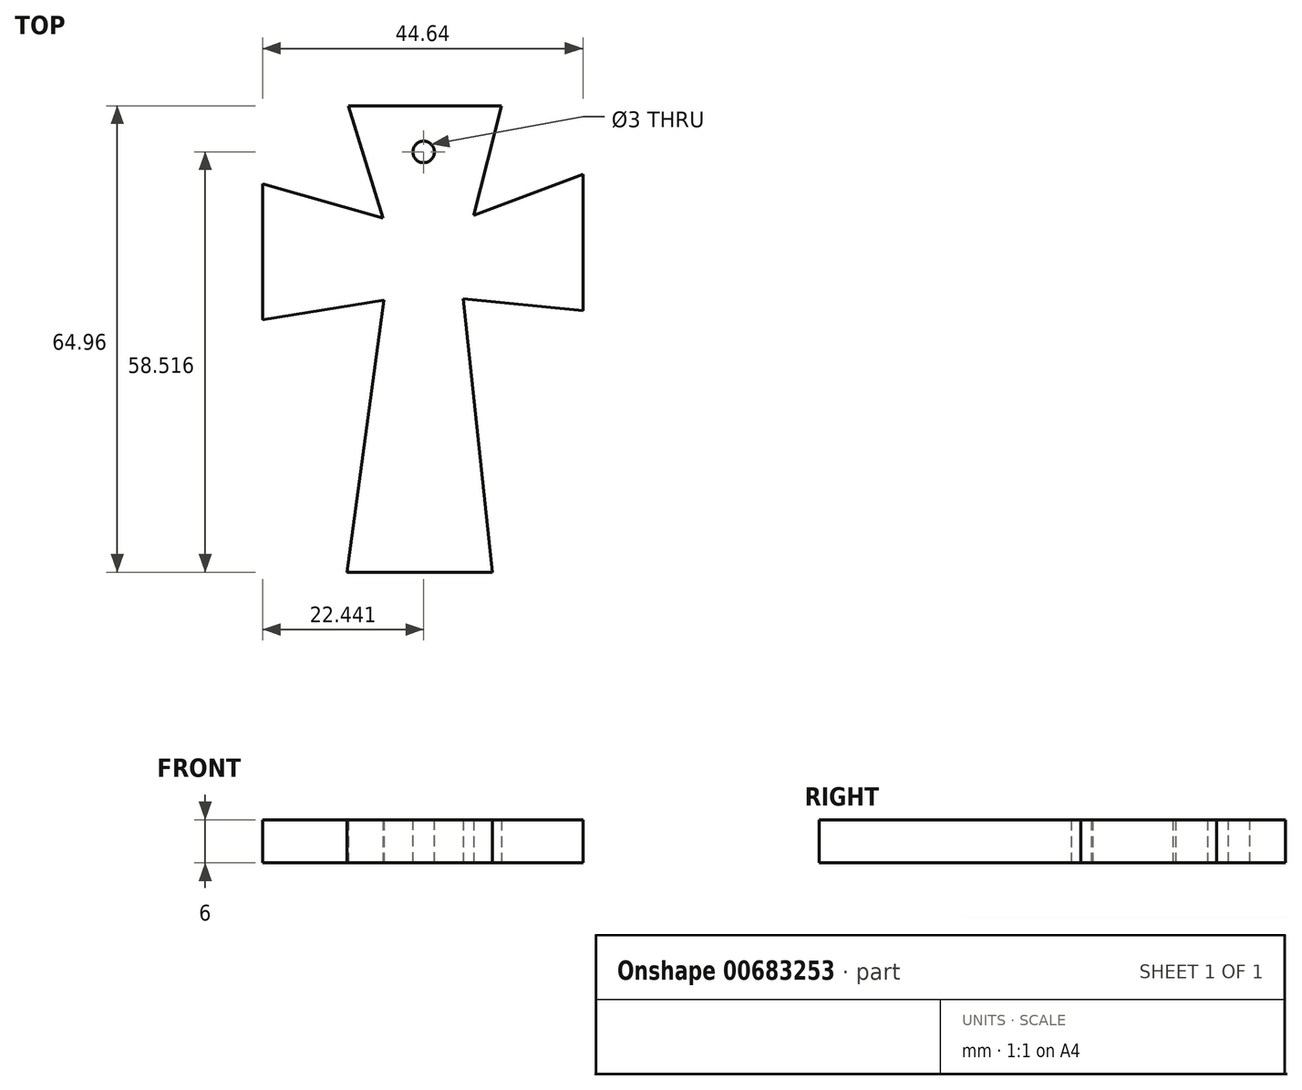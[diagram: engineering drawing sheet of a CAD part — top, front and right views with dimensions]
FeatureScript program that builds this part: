
annotation { "Feature Type Name" : "Feature", "Feature Type Description" : "" }
export const myFeature = defineFeature(function(context is Context, id is Id, definition is map)
    precondition{}
    {
        {
            var Q0;
            Q0=qCreatedBy(makeId("Top.planeOp"),FACE);
            var sketch = newSketch(context, id + "F0", { "sketchPlane" : qUnion([Q0])});
            skLineSegment(sketch, "E0", {"start": v(-27.71, 40.02) * mm, "end": v(-32.86, 2.12) * mm});
            skLineSegment(sketch, "E1", {"start": v(-32.86, 2.12) * mm, "end": v(-12.62, 2.12) * mm});
            skLineSegment(sketch, "E2", {"start": v(-12.62, 2.12) * mm, "end": v(-16.67, 40.2) * mm});
            skLineSegment(sketch, "E3", {"start": v(-16.67, 40.2) * mm, "end": v(0, 38.55) * mm});
            skLineSegment(sketch, "E4", {"start": v(0, 38.55) * mm, "end": v(0, 57.5) * mm});
            skLineSegment(sketch, "E5", {"start": v(0, 57.5) * mm, "end": v(-15.2, 51.8) * mm});
            skLineSegment(sketch, "E6", {"start": v(-15.2, 51.8) * mm, "end": v(-11.34, 67.08) * mm});
            skLineSegment(sketch, "E7", {"start": v(-11.34, 67.08) * mm, "end": v(-32.68, 67.08) * mm});
            skLineSegment(sketch, "E8", {"start": v(-32.68, 67.08) * mm, "end": v(-27.9, 51.43) * mm});
            skLineSegment(sketch, "E9", {"start": v(-27.9, 51.43) * mm, "end": v(-44.64, 56.21) * mm});
            skLineSegment(sketch, "E10", {"start": v(-44.64, 56.21) * mm, "end": v(-44.64, 37.26) * mm});
            skLineSegment(sketch, "E11", {"start": v(-44.64, 37.26) * mm, "end": v(-27.71, 40.02) * mm});
            skSolve(sketch);
        }
        {
            var Q0;
            Q0 = qSketchRegion(id + "F0", true);
            extrude(context, id + "F1", {"entities" : qUnion([Q0]), "depth" : 6 * mm, "offsetDistance" : 25 * mm});
        }
        {
            var Q0;
            Q0=makeQuery(id+"F1.opExtrude","CAP_FACE",FACE,{"disambiguationData":[OSD([sQuery(id+"F0.wireOp",EDGE,"E0"),sQuery(id+"F0.wireOp",EDGE,"E1"),sQuery(id+"F0.wireOp",EDGE,"E2"),sQuery(id+"F0.wireOp",EDGE,"E3"),sQuery(id+"F0.wireOp",EDGE,"E4"),sQuery(id+"F0.wireOp",EDGE,"E5"),sQuery(id+"F0.wireOp",EDGE,"E6"),sQuery(id+"F0.wireOp",EDGE,"E7"),sQuery(id+"F0.wireOp",EDGE,"E8"),sQuery(id+"F0.wireOp",EDGE,"E9"),sQuery(id+"F0.wireOp",EDGE,"E10"),sQuery(id+"F0.wireOp",EDGE,"E11")])],"isStart":false});
            var sketch = newSketch(context, id + "F2", { "sketchPlane" : qUnion([Q0])});
            skCircle(sketch, "E12", {"center": v(-22.2, 60.64) * mm, "radius": 1.96 * mm});
            skSolve(sketch);
        }
        {
            var Q0;
            Q0=sQuery(id+"F2.wireOp",VERTEX,"E12.center");
            var Q1;
            Q1=makeQuery(id+"F1.opExtrude","SWEPT_BODY",BODY,{"disambiguationData":[OSD([sQuery(id+"F0.wireOp",EDGE,"E0"),sQuery(id+"F0.wireOp",EDGE,"E1"),sQuery(id+"F0.wireOp",EDGE,"E2"),sQuery(id+"F0.wireOp",EDGE,"E3"),sQuery(id+"F0.wireOp",EDGE,"E4"),sQuery(id+"F0.wireOp",EDGE,"E5"),sQuery(id+"F0.wireOp",EDGE,"E6"),sQuery(id+"F0.wireOp",EDGE,"E7"),sQuery(id+"F0.wireOp",EDGE,"E8"),sQuery(id+"F0.wireOp",EDGE,"E9"),sQuery(id+"F0.wireOp",EDGE,"E10"),sQuery(id+"F0.wireOp",EDGE,"E11")])]});
            hole(context, id + "F3", {"style" : HoleStyle.SIMPLE, "endStyle" : HoleEndStyle.THROUGH, "holeDiameter" : 3 * mm, "majorDiameter" : 5 * mm, "isTappedThrough" : true, "tappedDepth" : 12 * mm, "tapClearance" : 3, "locations" : qUnion([Q0]), "scope" : qUnion([Q1])});
        }
    });
